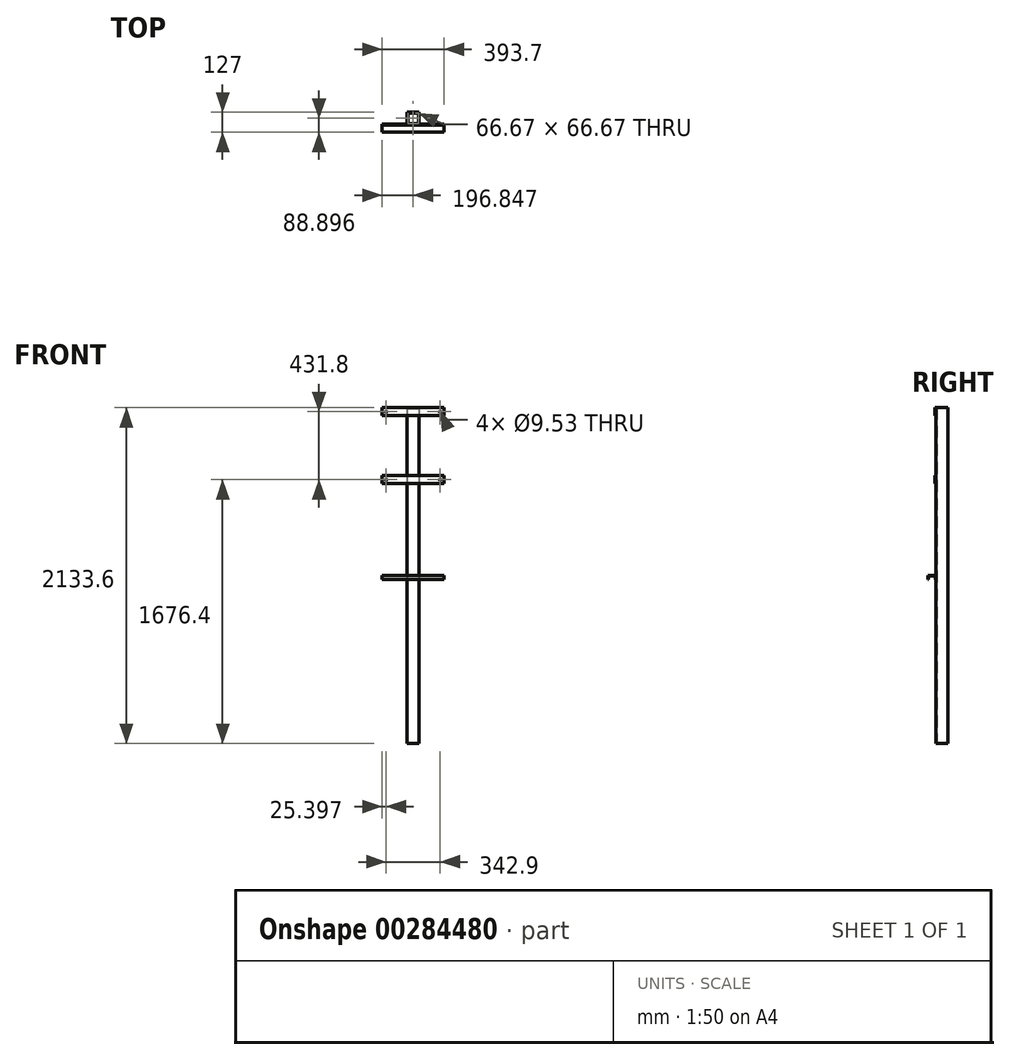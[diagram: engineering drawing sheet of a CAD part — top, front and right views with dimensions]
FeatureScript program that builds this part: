
annotation { "Feature Type Name" : "Feature", "Feature Type Description" : "" }
export const myFeature = defineFeature(function(context is Context, id is Id, definition is map)
    precondition{}
    {
        {
            var Q0;
            Q0=qCreatedBy(makeId("Top.planeOp"),FACE);
            var sketch = newSketch(context, id + "F0", { "sketchPlane" : qUnion([Q0])});
            skLineSegment(sketch, "E0.bottom", {"start": v(-38.12, 37.72) * mm, "end": v(38.08, 37.72) * mm});
            skLineSegment(sketch, "E0.top", {"start": v(-38.12, -38.48) * mm, "end": v(38.08, -38.48) * mm});
            skLineSegment(sketch, "E0.left", {"start": v(-38.12, 37.72) * mm, "end": v(-38.12, -38.48) * mm});
            skLineSegment(sketch, "E0.right", {"start": v(38.08, 37.72) * mm, "end": v(38.08, -38.48) * mm});
            skLineSegment(sketch, "E1.0", {"start": v(-33.36, 32.95) * mm, "end": v(-33.36, -33.72) * mm});
            skLineSegment(sketch, "E1.1", {"start": v(-33.36, 32.95) * mm, "end": v(33.31, 32.95) * mm});
            skLineSegment(sketch, "E1.2", {"start": v(33.31, 32.95) * mm, "end": v(33.31, -33.72) * mm});
            skLineSegment(sketch, "E1.3", {"start": v(-33.36, -33.72) * mm, "end": v(33.31, -33.72) * mm});
            skSolve(sketch);
        }
        {
            var Q0;
            Q0=makeQuery(id+"F0.imprint","IMPRINT",FACE,{"disambiguationData":[TD([[makeQuery(id+"F0.imprint","IMPRINT",EDGE,{"derivedFrom":sQuery(id+"F0.wireOp",EDGE,"E0.bottom")}),-1.0]])]});
            extrude(context, id + "F1", {"entities" : qUnion([Q0]), "depth" : 2133.6 * mm});
        }
        {
            var Q0;
            Q0=makeQuery(id+"F1.opExtrude","CAP_FACE",FACE,{"disambiguationData":[OSD([sQuery(id+"F0.wireOp",EDGE,"E0.bottom"),sQuery(id+"F0.wireOp",EDGE,"E0.top"),sQuery(id+"F0.wireOp",EDGE,"E0.left"),sQuery(id+"F0.wireOp",EDGE,"E0.right"),sQuery(id+"F0.wireOp",EDGE,"E1.0"),sQuery(id+"F0.wireOp",EDGE,"E1.1"),sQuery(id+"F0.wireOp",EDGE,"E1.2"),sQuery(id+"F0.wireOp",EDGE,"E1.3")])],"isStart":false});
            var sketch = newSketch(context, id + "F2", { "sketchPlane" : qUnion([Q0])});
            skSolve(sketch);
        }
        {
            var Q0;
            Q0=makeQuery(id+"F2.imprint","IMPRINT",FACE,{"disambiguationData":[TD([[makeQuery(id+"F2.imprint","IMPRINT",EDGE,{"derivedFrom":makeQuery(id+"F1.opExtrude","CAP_EDGE",EDGE,{"disambiguationData":[OSD([sQuery(id+"F0.wireOp",EDGE,"E1.0")])],"isStart":false})}),1.0]])]});
            var sketch = newSketch(context, id + "F3", { "sketchPlane" : qUnion([Q0])});
            skSolve(sketch);
        }
        {
            var Q0;
            Q0=qSketchRegion(id+"F3",true);
            var Q1;
            Q1=makeQuery(id+"F2.imprint","IMPRINT",FACE,{"disambiguationData":[TD([[makeQuery(id+"F2.imprint","IMPRINT",EDGE,{"derivedFrom":makeQuery(id+"F1.opExtrude","CAP_EDGE",EDGE,{"disambiguationData":[OSD([sQuery(id+"F0.wireOp",EDGE,"E1.0")])],"isStart":false})}),1.0]])]});
            extrude(context, id + "F4", {"entities" : qUnion([Q0, Q1]), "oppositeDirection" : true, "depth" : 4.76 * mm});
        }
        {
            var Q0;
            Q0=makeQuery(id+"F1.opExtrude","SWEPT_FACE",FACE,{"disambiguationData":[OSD([sQuery(id+"F0.wireOp",EDGE,"E0.top")])]});
            var sketch = newSketch(context, id + "F5", { "sketchPlane" : qUnion([Q0])});
            skLineSegment(sketch, "E2", {"start": v(-38.12, 2133.6) * mm, "end": v(-196.87, 2133.6) * mm});
            skLineSegment(sketch, "E3", {"start": v(-196.87, 2133.6) * mm, "end": v(-196.87, 2082.8) * mm});
            skLineSegment(sketch, "E4", {"start": v(-196.87, 2082.8) * mm, "end": v(196.83, 2082.8) * mm});
            skLineSegment(sketch, "E5", {"start": v(196.83, 2082.8) * mm, "end": v(196.83, 2133.6) * mm});
            skLineSegment(sketch, "E6", {"start": v(-38.12, 2133.6) * mm, "end": v(38.08, 2133.6) * mm});
            skLineSegment(sketch, "E7", {"start": v(38.08, 2133.6) * mm, "end": v(196.83, 2133.6) * mm});
            skCircle(sketch, "E8", {"center": v(-171.47, 2108.2) * mm, "radius": 4.76 * mm});
            skCircle(sketch, "E9", {"center": v(171.43, 2108.2) * mm, "radius": 4.76 * mm});
            skLineSegment(sketch, "E10", {"start": v(-196.87, 1701.8) * mm, "end": v(-38.12, 1701.8) * mm});
            skLineSegment(sketch, "E11", {"start": v(-38.12, 1701.8) * mm, "end": v(38.08, 1701.8) * mm});
            skLineSegment(sketch, "E12", {"start": v(38.08, 1701.8) * mm, "end": v(196.83, 1701.8) * mm});
            skLineSegment(sketch, "E13", {"start": v(196.83, 1701.8) * mm, "end": v(196.83, 1650.99) * mm});
            skLineSegment(sketch, "E14", {"start": v(196.83, 1650.99) * mm, "end": v(-196.87, 1650.99) * mm});
            skLineSegment(sketch, "E15", {"start": v(-196.87, 1650.99) * mm, "end": v(-196.87, 1701.8) * mm});
            skCircle(sketch, "E16", {"center": v(171.43, 1676.4) * mm, "radius": 4.76 * mm});
            skCircle(sketch, "E17", {"center": v(-171.47, 1676.4) * mm, "radius": 4.76 * mm});
            skSolve(sketch);
        }
        {
            var Q0;
            {var subQ1=sQuery(id+"F5.wireOp",EDGE,"E10");Q0=makeQuery(id+"F5.imprint","IMPRINT",FACE,{"disambiguationData":[TD([[makeQuery(id+"F5.imprint","IMPRINT",EDGE,{"derivedFrom":subQ1}),-1.0]])]});}
            var Q1;
            {var subQ4=sQuery(id+"F5.wireOp",EDGE,"E12");Q1=makeQuery(id+"F5.imprint","IMPRINT",FACE,{"disambiguationData":[TD([[makeQuery(id+"F5.imprint","IMPRINT",EDGE,{"derivedFrom":subQ4}),-1.0]])]});}
            var Q2;
            {var subQ0=sQuery(id+"F5.wireOp",EDGE,"E11");Q2=makeQuery(id+"F5.imprint","IMPRINT",FACE,{"disambiguationData":[TD([[makeQuery(id+"F5.imprint","IMPRINT",EDGE,{"derivedFrom":subQ0}),-1.0]])]});}
            var Q3;
            {var subQ4=sQuery(id+"F5.wireOp",EDGE,"E2");Q3=makeQuery(id+"F5.imprint","IMPRINT",FACE,{"disambiguationData":[TD([[makeQuery(id+"F5.imprint","IMPRINT",EDGE,{"derivedFrom":subQ4}),1.0]])]});}
            var Q4;
            {var subQ6=sQuery(id+"F5.wireOp",EDGE,"E6");Q4=makeQuery(id+"F5.imprint","IMPRINT",FACE,{"disambiguationData":[TD([[makeQuery(id+"F5.imprint","IMPRINT",EDGE,{"derivedFrom":subQ6}),-1.0]])]});}
            var Q5;
            {var subQ1=sQuery(id+"F5.wireOp",EDGE,"E5");Q5=makeQuery(id+"F5.imprint","IMPRINT",FACE,{"disambiguationData":[TD([[makeQuery(id+"F5.imprint","IMPRINT",EDGE,{"derivedFrom":subQ1}),1.0]])]});}
            extrude(context, id + "F6", {"entities" : qUnion([Q0, Q1, Q2, Q3, Q4, Q5]), "operationType" : NewBodyOperationType.ADD, "depth" : 6.35 * mm});
        }
        {
            var Q0;
            Q0=makeQuery(id+"F1.opExtrude","SWEPT_FACE",FACE,{"disambiguationData":[OSD([sQuery(id+"F0.wireOp",EDGE,"E0.right")])]});
            var sketch = newSketch(context, id + "F7", { "sketchPlane" : qUnion([Q0])});
            skLineSegment(sketch, "E18", {"start": v(-38.48, 1066.8) * mm, "end": v(-89.28, 1066.8) * mm});
            skLineSegment(sketch, "E19", {"start": v(-89.28, 1066.8) * mm, "end": v(-89.28, 1041.4) * mm});
            skLineSegment(sketch, "E20", {"start": v(-89.28, 1041.4) * mm, "end": v(-86.1, 1041.4) * mm});
            skLineSegment(sketch, "E21", {"start": v(-86.1, 1041.4) * mm, "end": v(-86.1, 1063.62) * mm});
            skLineSegment(sketch, "E22", {"start": v(-86.1, 1063.62) * mm, "end": v(-41.66, 1063.62) * mm});
            skLineSegment(sketch, "E23", {"start": v(-41.66, 1063.62) * mm, "end": v(-41.66, 1041.4) * mm});
            skLineSegment(sketch, "E24", {"start": v(-41.66, 1041.4) * mm, "end": v(-38.48, 1041.4) * mm});
            skSolve(sketch);
        }
        {
            var Q0;
            Q0=qSketchRegion(id+"F7",true);
            var Q1;
            {var subQ0=sQuery(id+"F7.wireOp",EDGE,"E18");Q1=makeQuery(id+"F7.imprint","IMPRINT",FACE,{"disambiguationData":[TD([[makeQuery(id+"F7.imprint","IMPRINT",EDGE,{"derivedFrom":subQ0}),1.0]])]});}
            var Q2;
            {var subQ0=sQuery(id+"F7.wireOp",EDGE,"kfeQCSjW-MuyM-jiYT-dt5S-AhHptrX4ySRa");Q2=makeQuery(id+"F7.imprint","IMPRINT",FACE,{"disambiguationData":[TD([[makeQuery(id+"F7.imprint","IMPRINT",EDGE,{"derivedFrom":subQ0}),-1.0]])]});}
            extrude(context, id + "F8", {"entities" : qUnion([Q0, Q1, Q2]), "depth" : 158.75 * mm, "hasSecondDirection" : true, "secondDirectionOppositeDirection" : true, "secondDirectionDepth" : 234.95 * mm});
        }
    });
